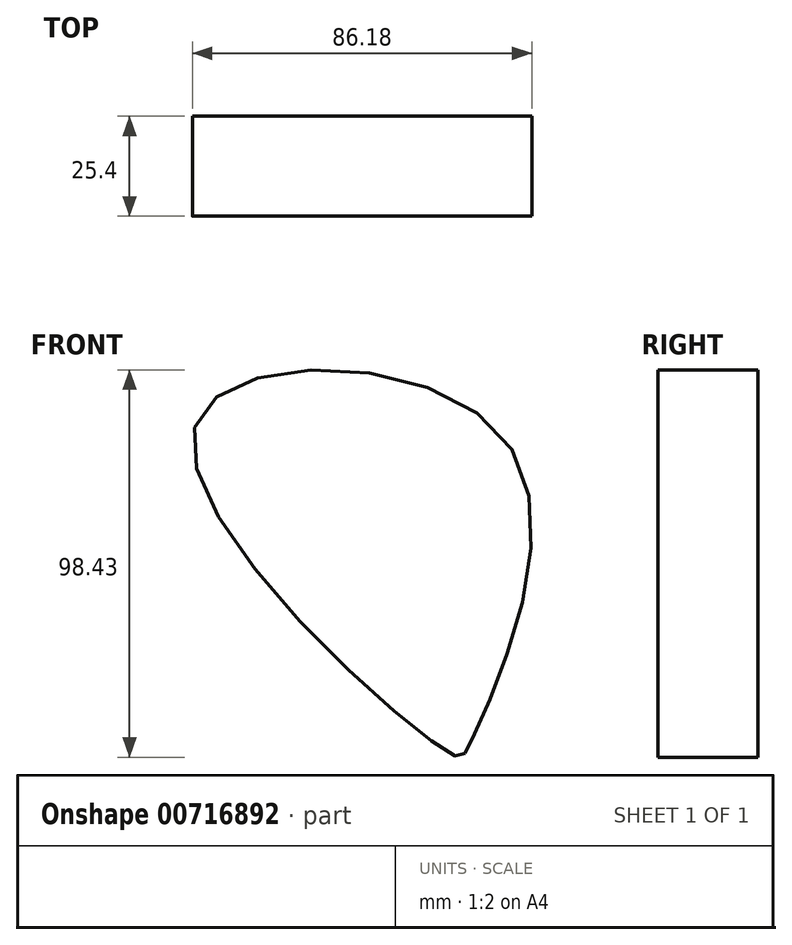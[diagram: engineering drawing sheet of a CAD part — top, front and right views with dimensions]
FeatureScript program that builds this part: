
annotation { "Feature Type Name" : "Feature", "Feature Type Description" : "" }
export const myFeature = defineFeature(function(context is Context, id is Id, definition is map)
    precondition{}
    {
        {
            var Q0;
            Q0=qCreatedBy(makeId("Front.planeOp"),FACE);
            var sketch = newSketch(context, id + "F0", { "sketchPlane" : qUnion([Q0])});
            skFitSpline(sketch, "E0", {"points": [v(-40.05, 44.38) * mm, v(25.51, -38.81) * mm, v(29.53, -36.65) * mm, v(39.12, 40.98) * mm, v(-40.05, 44.38) * mm]});
            skSolve(sketch);
        }
        {
            var Q0;
            Q0=makeQuery(id+"F0.imprint","IMPRINT",FACE,{"disambiguationData":[TD([[makeQuery(id+"F0.imprint","IMPRINT",EDGE,{"derivedFrom":sQuery(id+"F0.wireOp",EDGE,"E0")}),1.0]])]});
            extrude(context, id + "F1", {"entities" : qUnion([Q0]), "depth" : 25.4 * mm, "offsetDistance" : 25.4 * mm});
        }
    });
